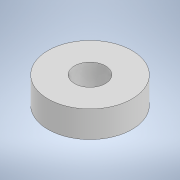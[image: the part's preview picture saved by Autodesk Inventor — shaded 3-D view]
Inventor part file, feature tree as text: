
AUTODESK INVENTOR PART (.ipt)
format: ipt  version: 2020 (Build 240168000, 168)  size: 96,256 bytes
history: native  units: mm
features: other x1, extrude x1, sketch x1
ambient origin geometry x8: Origin, YZ Plane, XZ Plane, XY Plane, X Axis, Y Axis, Z Axis, Center Point
bodies: Body1 (feature_tree)
feature tree (3):
  other  "Твердое тело1"
  extrude  "Выдавливание1"  Depth=3.5mm
  sketch  "Эскиз1"
